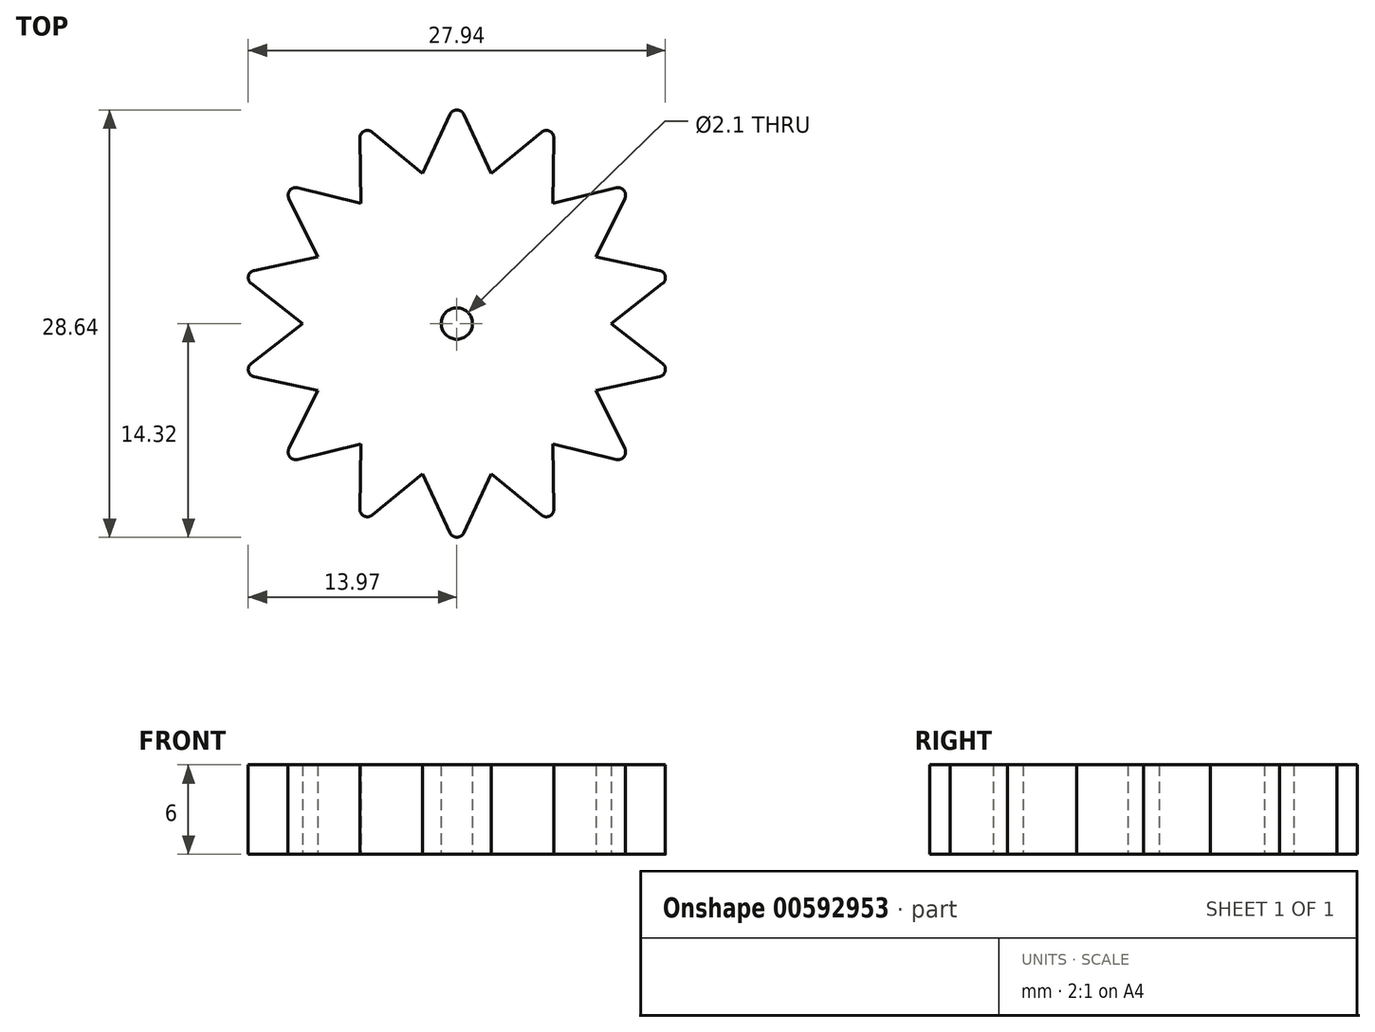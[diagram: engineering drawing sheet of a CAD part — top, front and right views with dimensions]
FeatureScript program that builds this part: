
annotation { "Feature Type Name" : "Feature", "Feature Type Description" : "" }
export const myFeature = defineFeature(function(context is Context, id is Id, definition is map)
    precondition{}
    {
        {
            var Q0;
            Q0=qCreatedBy(makeId("Top.planeOp"),FACE);
            var sketch = newSketch(context, id + "F0", { "sketchPlane" : qUnion([Q0])});
            skCircle(sketch, "E0", {"center": v(0, 0) * mm, "radius": 1.05 * mm});
            skLineSegment(sketch, "E1", {"start": v(0, -10) * mm, "end": v(0, -15) * mm, "construction": true});
            skLineSegment(sketch, "E2", {"start": v(-0.45, -14.03) * mm, "end": v(-2.48, -9.69) * mm});
            skLineSegment(sketch, "E3", {"start": v(0.45, -14.03) * mm, "end": v(2.48, -9.69) * mm});
            skLineSegment(sketch, "E4.1.0", {"start": v(5.68, -12.84) * mm, "end": v(1.97, -9.8) * mm});
            skLineSegment(sketch, "E4.1.1", {"start": v(6.5, -12.44) * mm, "end": v(6.44, -7.65) * mm});
            skLineSegment(sketch, "E4.2.0", {"start": v(10.69, -9.1) * mm, "end": v(6.03, -7.98) * mm});
            skLineSegment(sketch, "E4.2.1", {"start": v(11.25, -8.4) * mm, "end": v(9.12, -4.1) * mm});
            skLineSegment(sketch, "E4.3.0", {"start": v(13.58, -3.56) * mm, "end": v(8.9, -4.57) * mm});
            skLineSegment(sketch, "E4.3.1", {"start": v(13.78, -2.68) * mm, "end": v(10, 0.26) * mm});
            skLineSegment(sketch, "E4.4.0", {"start": v(13.78, 2.68) * mm, "end": v(10, -0.26) * mm});
            skLineSegment(sketch, "E4.4.1", {"start": v(13.58, 3.56) * mm, "end": v(8.9, 4.57) * mm});
            skLineSegment(sketch, "E4.5.0", {"start": v(11.25, 8.4) * mm, "end": v(9.12, 4.1) * mm});
            skLineSegment(sketch, "E4.5.1", {"start": v(10.69, 9.1) * mm, "end": v(6.03, 7.98) * mm});
            skLineSegment(sketch, "E4.6.0", {"start": v(6.5, 12.44) * mm, "end": v(6.44, 7.65) * mm});
            skLineSegment(sketch, "E4.6.1", {"start": v(5.68, 12.84) * mm, "end": v(1.97, 9.8) * mm});
            skLineSegment(sketch, "E4.7.0", {"start": v(0.45, 14.03) * mm, "end": v(2.48, 9.69) * mm});
            skLineSegment(sketch, "E4.7.1", {"start": v(-0.45, 14.03) * mm, "end": v(-2.48, 9.69) * mm});
            skLineSegment(sketch, "E4.8.0", {"start": v(-5.68, 12.84) * mm, "end": v(-1.97, 9.8) * mm});
            skLineSegment(sketch, "E4.8.1", {"start": v(-6.5, 12.44) * mm, "end": v(-6.44, 7.65) * mm});
            skLineSegment(sketch, "E4.9.0", {"start": v(-10.69, 9.1) * mm, "end": v(-6.03, 7.98) * mm});
            skLineSegment(sketch, "E4.9.1", {"start": v(-11.25, 8.4) * mm, "end": v(-9.12, 4.1) * mm});
            skLineSegment(sketch, "E4.10.0", {"start": v(-13.58, 3.56) * mm, "end": v(-8.9, 4.57) * mm});
            skLineSegment(sketch, "E4.10.1", {"start": v(-13.78, 2.68) * mm, "end": v(-10, -0.26) * mm});
            skLineSegment(sketch, "E4.11.0", {"start": v(-13.78, -2.68) * mm, "end": v(-10, 0.26) * mm});
            skLineSegment(sketch, "E4.11.1", {"start": v(-13.58, -3.56) * mm, "end": v(-8.9, -4.57) * mm});
            skLineSegment(sketch, "E4.12.0", {"start": v(-11.25, -8.4) * mm, "end": v(-9.12, -4.1) * mm});
            skLineSegment(sketch, "E4.12.1", {"start": v(-10.69, -9.1) * mm, "end": v(-6.03, -7.98) * mm});
            skLineSegment(sketch, "E4.13.0", {"start": v(-6.5, -12.44) * mm, "end": v(-6.44, -7.65) * mm});
            skLineSegment(sketch, "E4.13.1", {"start": v(-5.68, -12.84) * mm, "end": v(-1.97, -9.8) * mm});
            skPoint(sketch, "E5.visualSharp", {"position": v(6.5, -13.51) * mm});
            skArc(sketch, "E5.filletArc", {"start": v(5.68, -12.84) * mm, "mid": v(6.21, -12.9) * mm, "end": v(6.5, -12.44) * mm});
            skPoint(sketch, "E6.visualSharp", {"position": v(11.73, -9.35) * mm});
            skArc(sketch, "E6.filletArc", {"start": v(10.69, -9.1) * mm, "mid": v(11.2, -8.93) * mm, "end": v(11.25, -8.4) * mm});
            skPoint(sketch, "E7.visualSharp", {"position": v(14.62, -3.34) * mm});
            skArc(sketch, "E7.filletArc", {"start": v(13.58, -3.56) * mm, "mid": v(13.96, -3.19) * mm, "end": v(13.78, -2.68) * mm});
            skPoint(sketch, "E8.visualSharp", {"position": v(14.62, 3.34) * mm});
            skArc(sketch, "E8.filletArc", {"start": v(13.78, 2.68) * mm, "mid": v(13.96, 3.19) * mm, "end": v(13.58, 3.56) * mm});
            skPoint(sketch, "E9.visualSharp", {"position": v(11.73, 9.35) * mm});
            skArc(sketch, "E9.filletArc", {"start": v(11.25, 8.4) * mm, "mid": v(11.2, 8.93) * mm, "end": v(10.69, 9.1) * mm});
            skPoint(sketch, "E10.visualSharp", {"position": v(6.5, 13.51) * mm});
            skArc(sketch, "E10.filletArc", {"start": v(6.5, 12.44) * mm, "mid": v(6.21, 12.9) * mm, "end": v(5.68, 12.84) * mm});
            skPoint(sketch, "E11.visualSharp", {"position": v(0, 15) * mm});
            skArc(sketch, "E11.filletArc", {"start": v(0.45, 14.03) * mm, "mid": v(0, 14.32) * mm, "end": v(-0.45, 14.03) * mm});
            skPoint(sketch, "E12.visualSharp", {"position": v(-6.5, 13.51) * mm});
            skArc(sketch, "E12.filletArc", {"start": v(-5.68, 12.84) * mm, "mid": v(-6.21, 12.9) * mm, "end": v(-6.5, 12.44) * mm});
            skPoint(sketch, "E13.visualSharp", {"position": v(-11.73, 9.35) * mm});
            skArc(sketch, "E13.filletArc", {"start": v(-10.69, 9.1) * mm, "mid": v(-11.2, 8.93) * mm, "end": v(-11.25, 8.4) * mm});
            skPoint(sketch, "E14.visualSharp", {"position": v(-14.62, 3.34) * mm});
            skArc(sketch, "E14.filletArc", {"start": v(-13.58, 3.56) * mm, "mid": v(-13.96, 3.19) * mm, "end": v(-13.78, 2.68) * mm});
            skPoint(sketch, "E15.visualSharp", {"position": v(-14.62, -3.34) * mm});
            skArc(sketch, "E15.filletArc", {"start": v(-13.78, -2.68) * mm, "mid": v(-13.96, -3.19) * mm, "end": v(-13.58, -3.56) * mm});
            skPoint(sketch, "E16.visualSharp", {"position": v(-11.73, -9.35) * mm});
            skArc(sketch, "E16.filletArc", {"start": v(-11.25, -8.4) * mm, "mid": v(-11.2, -8.93) * mm, "end": v(-10.69, -9.1) * mm});
            skPoint(sketch, "E17.visualSharp", {"position": v(-6.5, -13.51) * mm});
            skArc(sketch, "E17.filletArc", {"start": v(-6.5, -12.44) * mm, "mid": v(-6.21, -12.9) * mm, "end": v(-5.68, -12.84) * mm});
            skPoint(sketch, "E18.visualSharp", {"position": v(0, -15) * mm});
            skArc(sketch, "E18.filletArc", {"start": v(-0.45, -14.03) * mm, "mid": v(0, -14.32) * mm, "end": v(0.45, -14.03) * mm});
            skSolve(sketch);
        }
        {
            var Q0;
            Q0=makeQuery(id+"F0.imprint","IMPRINT",FACE,{"disambiguationData":[TD([[makeQuery(id+"F0.imprint","IMPRINT",EDGE,{"derivedFrom":sQuery(id+"F0.wireOp",EDGE,"E0")}),-1.0]])]});
            extrude(context, id + "F1", {"entities" : qUnion([Q0]), "depth" : 6 * mm, "offsetDistance" : 25 * mm});
        }
    });
